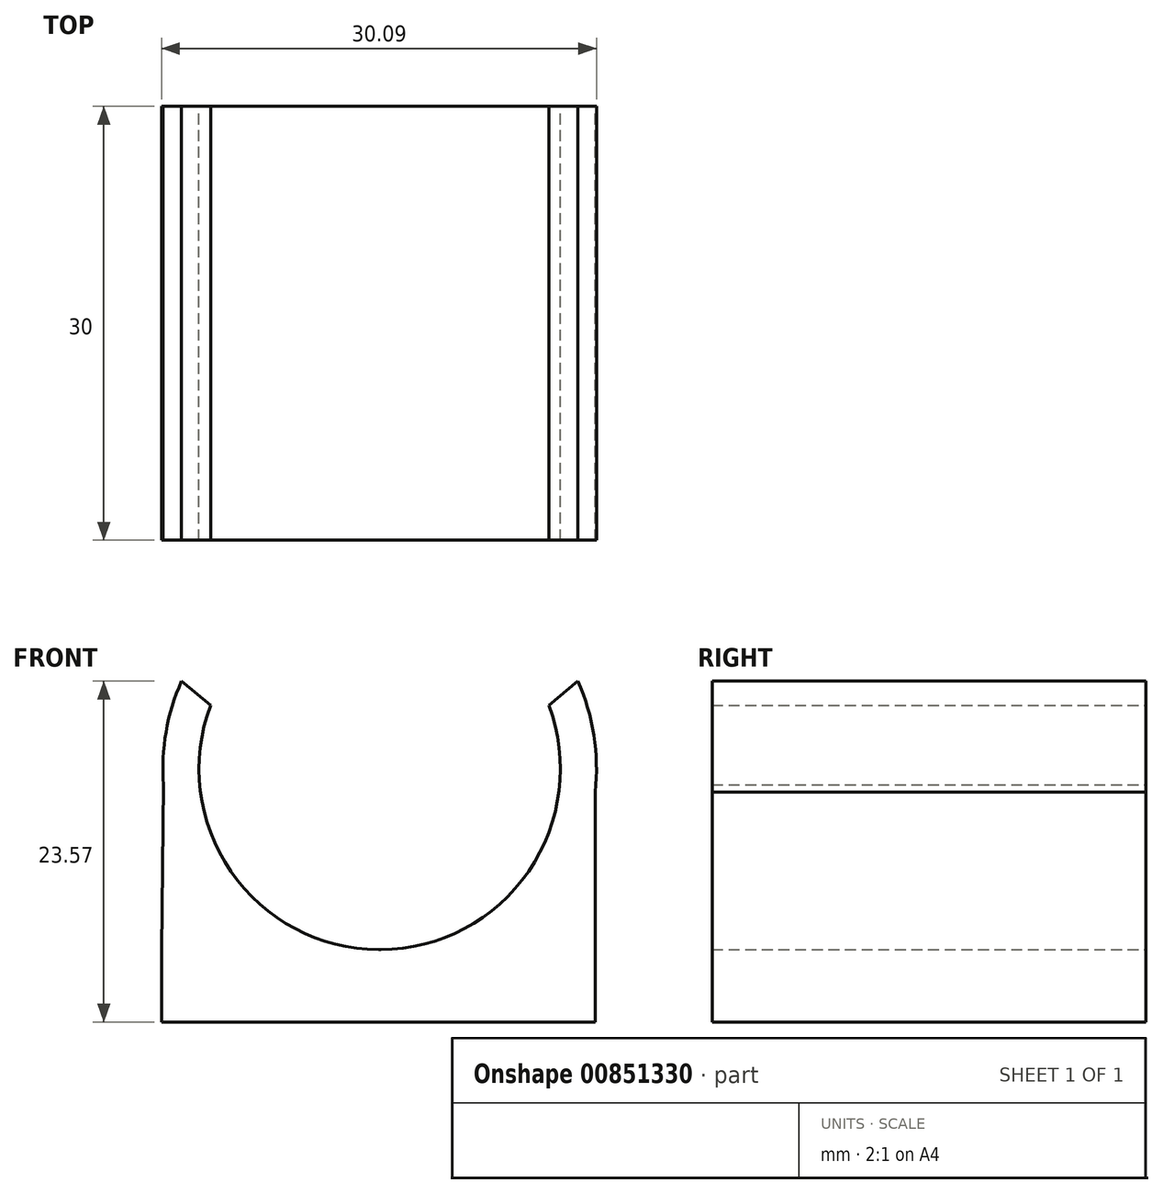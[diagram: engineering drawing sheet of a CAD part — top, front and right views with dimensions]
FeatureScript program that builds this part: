
annotation { "Feature Type Name" : "Feature", "Feature Type Description" : "" }
export const myFeature = defineFeature(function(context is Context, id is Id, definition is map)
    precondition{}
    {
        {
            var Q0;
            Q0=qCreatedBy(makeId("Front.planeOp"),FACE);
            var sketch = newSketch(context, id + "F0", { "sketchPlane" : qUnion([Q0])});
            skLineSegment(sketch, "E0.bottom", {"start": v(-13.24, 0) * mm, "end": v(-43.24, 0) * mm});
            skLineSegment(sketch, "E0.top", {"start": v(-28.07, 5) * mm, "end": v(-28.24, 5) * mm});
            skLineSegment(sketch, "E0.left", {"start": v(-13.24, 0) * mm, "end": v(-13.24, 5) * mm});
            skLineSegment(sketch, "E0.right", {"start": v(-43.24, 0) * mm, "end": v(-43.24, 5) * mm});
            skArc(sketch, "E1", {"start": v(-39.85, 21.9) * mm, "mid": v(-28.15, 5) * mm, "end": v(-16.45, 21.9) * mm});
            skPoint(sketch, "E1.first.point", {"position": v(-28.24, 5) * mm});
            skPoint(sketch, "E1.second.point", {"position": v(-28.24, 30) * mm});
            skPoint(sketch, "E1.second.point.positionSnap0", {"position": v(-28.24, 5) * mm});
            skPoint(sketch, "E1.third.point", {"position": v(-16.45, 21.9) * mm});
            skArc(sketch, "E2", {"start": v(-41.87, 23.57) * mm, "mid": v(-42.93, 20.06) * mm, "end": v(-43.11, 16.4) * mm});
            skLineSegment(sketch, "E3", {"start": v(-43.24, 5) * mm, "end": v(-43.08, 18.94) * mm});
            skLineSegment(sketch, "E4", {"start": v(-13.24, 5) * mm, "end": v(-13.24, 19.1) * mm});
            skLineSegment(sketch, "E5", {"start": v(-39.85, 21.9) * mm, "end": v(-41.87, 23.57) * mm});
            skArc(sketch, "E6.trimOffspring", {"start": v(-13.24, 15.9) * mm, "mid": v(-13.33, 19.82) * mm, "end": v(-14.44, 23.57) * mm});
            skLineSegment(sketch, "E7", {"start": v(-39.85, 21.9) * mm, "end": v(-16.45, 21.9) * mm, "construction": true});
            skLineSegment(sketch, "E8", {"start": v(-16.45, 21.9) * mm, "end": v(-14.44, 23.57) * mm});
            skLineSegment(sketch, "E9", {"start": v(-41.87, 23.57) * mm, "end": v(-14.44, 23.57) * mm, "construction": true});
            skSolve(sketch);
        }
        {
            var Q0;
            Q0 = qSketchRegion(id + "F0", true);
            extrude(context, id + "F1", {"entities" : qUnion([Q0]), "depth" : 30 * mm, "offsetDistance" : 25 * mm});
        }
    });
